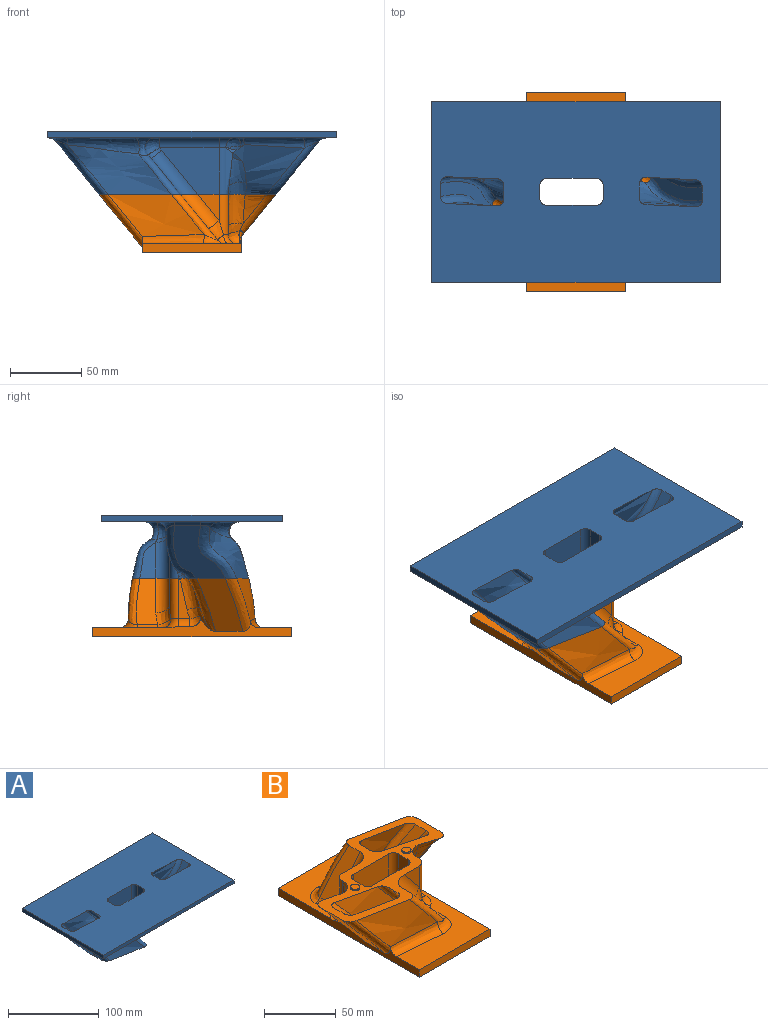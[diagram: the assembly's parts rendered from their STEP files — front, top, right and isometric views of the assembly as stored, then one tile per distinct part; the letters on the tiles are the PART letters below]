
ASSEMBLY  parts=2 mates=1
PART A: 89 faces, bbox 208.2x130.3x60.3 mm
  f0: plane 203.2x127mm, normal (0,0,-1), area 16715.4mm2, adj f4,f5,f6,f7,f62,f63,f64,f65
  f1: plane 27.1x22.42mm, normal (-0.78,0,0.63), area 270.1mm2, adj f20,f60,f84
  f2: bspline ~26.47x26.15mm, area 3.7mm2, adj f25,f52,f74
  f3: plane 0.85x0.52mm, normal (-1,0,0), area 0.2mm2, adj f11,f54,f84
  f4: plane 203.2x4.75mm, normal (0,1,0), area 965.2mm2, adj f0,f5,f7,f8
  f5: plane 127x4.75mm, normal (1,0,0), area 603.2mm2, adj f0,f4,f6,f8
  f6: plane 203.2x4.75mm, normal (0,-1,0), area 965.2mm2, adj f0,f5,f7,f8
  f7: plane 127x4.75mm, normal (-1,0,0), area 603.2mm2, adj f0,f4,f6,f8
  f8: plane 203.45x127.25mm, normal (0,0,1), area 23325.4mm2, adj f4,f5,f6,f7,f28,f29,f30,f31
  f9: cylinder r=6.35mm len=32.72mm, axis (0,0,-1), area 257.4mm2, adj f10,f13,f57,f58,f75,f84
  f10: plane 41.74x32.72mm, normal (0,-1,0), area 926.6mm2, adj f9,f55,f56,f77,f84
  f11: cylinder r=6.35mm len=32.72mm, axis (0,0,-1), area 241.2mm2, adj f3,f12,f52,f53,f70,f84
  f12: plane 41.72x32.72mm, normal (0,1,0), area 926.6mm2, adj f11,f60,f61,f68,f84
  f13: plane 4.33x2.1mm, normal (1,0,0), area 4.6mm2, adj f9,f59,f84
  f14: bspline ~26.57x26.16mm, area 3.1mm2, adj f15,f57,f71
  f15: bspline ~81.71x47.4mm, area 1132.1mm2, adj f14,f16,f58,f59,f69,f84
  f16: bspline ~51.16x47.96mm, area 420.9mm2, adj f15,f17,f67,f84
  f17: plane 37.97x37.8mm, normal (0.78,0,-0.63), area 979.7mm2, adj f16,f18,f65,f84
  f18: bspline ~52.84x48.18mm, area 451.5mm2, adj f17,f19,f63,f84
  f19: bspline ~85.74x51.46mm, area 1511.6mm2, adj f18,f20,f62,f84
  f20: bspline ~31.16x30.47mm, area 324.5mm2, adj f1,f19,f61,f64,f84
  f21: bspline ~53.3x48.55mm, area 461.5mm2, adj f22,f27,f82,f84
  f22: bspline ~80.68x45.46mm, area 1516.6mm2, adj f21,f26,f83,f84
  f23: plane 27.06x22.41mm, normal (0.78,0,0.63), area 191.7mm2, adj f26,f55,f84
  f24: bspline ~50.92x47.77mm, area 424.9mm2, adj f25,f27,f78,f84
  f25: bspline ~84.85x50.64mm, area 1089.3mm2, adj f2,f24,f53,f54,f76,f84
  f26: bspline ~31.1x30.41mm, area 312.9mm2, adj f22,f23,f56,f81,f84
  f27: plane 38.12x36.94mm, normal (-0.78,0,-0.63), area 981.5mm2, adj f21,f24,f80,f84
  f28: plane 44.45x9.53mm, normal (1,0,0), area 423.4mm2, adj f8,f29,f35,f84
  f29: cylinder r=4.76mm len=44.45mm, axis (0,0,-1), area 332.5mm2, adj f8,f28,f30,f84
  f30: plane 44.45x34.93mm, normal (0,-1,0), area 1552.4mm2, adj f8,f29,f31,f84
  f31: cylinder r=4.76mm len=44.45mm, axis (0,0,-1), area 332.5mm2, adj f8,f30,f32,f84
  f32: plane 44.45x9.53mm, normal (-1,0,0), area 423.4mm2, adj f8,f31,f33,f84
  f33: cylinder r=4.76mm len=44.45mm, axis (0,0,-1), area 332.5mm2, adj f8,f32,f34,f84
  f34: plane 44.45x34.93mm, normal (0,1,0), area 1552.4mm2, adj f8,f33,f35,f84
  f35: cylinder r=4.76mm len=44.45mm, axis (0,0,-1), area 332.5mm2, adj f8,f28,f34,f84
  f36: bspline ~80.13x56.1mm, area 1676.3mm2, adj f8,f37,f39,f84
  f37: bspline ~45.96x41.08mm, area 416.8mm2, adj f8,f36,f38,f84
  f38: plane 45.43x37.2mm, normal (-0.78,0,-0.63), area 587.4mm2, adj f8,f37,f40,f84
  f39: bspline ~56.3x50.6mm, area 399.9mm2, adj f8,f36,f43,f84
  f40: bspline ~53.19x48.1mm, area 414.1mm2, adj f8,f38,f41,f84
  f41: bspline ~77.52x52.9mm, area 1682.4mm2, adj f8,f40,f42,f84
  f42: bspline ~45.92x40.98mm, area 421.9mm2, adj f8,f41,f43,f84
  f43: plane 45.21x36.98mm, normal (0.78,0,0.63), area 581.6mm2, adj f8,f39,f42,f84
  f44: bspline ~74.38x49.37mm, area 1685mm2, adj f8,f45,f49,f84
  f45: bspline ~55.24x49.24mm, area 420mm2, adj f8,f44,f46,f84
  f46: plane 44.91x36.68mm, normal (0.78,0,-0.63), area 598.6mm2, adj f8,f45,f50,f84
  f47: bspline ~46.01x40.98mm, area 419.8mm2, adj f8,f48,f51,f84
  f48: plane 45.17x36.93mm, normal (-0.78,0,0.63), area 580.4mm2, adj f8,f47,f49,f84
  f49: bspline ~49.59x45.11mm, area 399.8mm2, adj f8,f44,f48,f84
  f50: bspline ~45.74x42.03mm, area 421.3mm2, adj f8,f46,f51,f84
  f51: bspline ~77.16x52.45mm, area 1689.8mm2, adj f8,f47,f50,f84
  f52: bspline ~10.59x8.46mm, area 46mm2, adj f2,f11,f53,f72
  f53: bspline ~32.83x16.02mm, area 369.8mm2, adj f11,f25,f52,f54
  f54: bspline ~13.55x12.77mm, area 82.6mm2, adj f3,f25,f53,f84
  f55: cylinder r=9.53mm len=37.14mm, axis (0.63,0,-0.78), area 542.6mm2, adj f10,f23,f56,f84
  f56: bspline ~19.85x18.08mm, area 39.9mm2, adj f10,f26,f55,f79
  f57: bspline ~11.14x7.85mm, area 43.8mm2, adj f9,f14,f73
  f58: bspline ~29.23x17.21mm, area 0mm2, adj f9,f15,f59
  f59: bspline ~16.03x15.49mm, area 128.9mm2, adj f13,f15,f58,f84
  f60: cylinder r=9.53mm len=37.33mm, axis (-0.63,0,-0.78), area 546.2mm2, adj f1,f12,f61,f84
  f61: bspline ~19.57x17.96mm, area 37.4mm2, adj f12,f20,f60,f66
  f62: bspline ~68.57x22.97mm, area 645.5mm2, adj f0,f19,f63,f64
  f63: bspline ~15.03x14.25mm, area 125.7mm2, adj f0,f18,f62,f65
  f64: bspline ~22.36x20.15mm, area 163.7mm2, adj f0,f20,f62,f66
  f65: cylinder r=6.99mm len=18.5mm, axis (0,-1,0), area 114.6mm2, adj f0,f17,f63,f67
  f66: bspline ~22.78x12.09mm, area 162mm2, adj f0,f61,f64,f68
  f67: bspline ~16.67x12.75mm, area 143.1mm2, adj f0,f16,f65,f69
  f68: cylinder r=6.99mm len=41.71mm, axis (-1,0,0), area 457.7mm2, adj f0,f12,f66,f70
  f69: bspline ~58x14.02mm, area 427.1mm2, adj f0,f15,f67,f71
  f70: torus R=13.33mm, axis (0,0,-1), area 76.6mm2, adj f0,f11,f68,f72
  f71: bspline ~8.55x8.16mm, area 29.4mm2, adj f0,f14,f69,f73
  f72: bspline ~13.61x8.18mm, area 85.8mm2, adj f0,f52,f70,f74
  f73: bspline ~13.15x8.04mm, area 86.3mm2, adj f0,f57,f71,f75
  f74: bspline ~8.96x8.54mm, area 33.4mm2, adj f0,f2,f72,f76
  f75: torus R=13.33mm, axis (0,0,-1), area 82.6mm2, adj f0,f9,f73,f77
  f76: bspline ~62.1x14.39mm, area 444mm2, adj f0,f25,f74,f78
  f77: cylinder r=6.99mm len=41.73mm, axis (1,0,0), area 457.9mm2, adj f0,f10,f75,f79
  f78: bspline ~17.07x12.87mm, area 151.7mm2, adj f0,f24,f76,f80
  f79: bspline ~22.42x12.24mm, area 162.6mm2, adj f0,f56,f77,f81
  f80: cylinder r=6.99mm len=18.32mm, axis (0,1,0), area 113.5mm2, adj f0,f27,f78,f82
  f81: bspline ~21.42x20.29mm, area 158.4mm2, adj f0,f26,f79,f83
  f82: bspline ~13.99x13.25mm, area 108.2mm2, adj f0,f21,f80,f83
  f83: bspline ~65.57x22.1mm, area 631.4mm2, adj f0,f22,f81,f82
  f84: plane 127.7x85.1mm, normal (0,0,-1), area 2652.4mm2, adj f1,f3,f9,f10,f11,f12,f13,f15
  f85: cylinder r=3.24mm len=6.48mm, axis (0,0,-1), area 25.8mm2, adj f84,f86
  f86: plane 6.48x6.48mm, normal (0,0,-1), area 32.9mm2, adj f85
  f87: cylinder r=3.24mm len=6.48mm, axis (0,0,-1), area 25.8mm2, adj f84,f88
  f88: plane 6.48x6.48mm, normal (0,0,-1), area 32.9mm2, adj f87
PART B: 86 faces, bbox 138.6x145.9x60.1 mm
  f0: plane 34.07x28.03mm, normal (-0.78,0,0.63), area 551.8mm2, adj f12,f47,f60,f76,f81
  f1: plane 28.58x7.98mm, normal (-1,0,0), area 124.8mm2, adj f4,f44,f56,f79,f81
  f2: cylinder r=6.35mm len=28.58mm, axis (0,0,-1), area 267.3mm2, adj f3,f6,f58,f66,f81
  f3: plane 18.4x15mm, normal (0,-1,0), area 138mm2, adj f2,f45,f81
  f4: cylinder r=6.35mm len=28.58mm, axis (0,0,-1), area 267.3mm2, adj f1,f5,f60,f78,f81
  f5: plane 18.4x15mm, normal (0,1,0), area 138mm2, adj f4,f47,f81
  f6: plane 28.58x9.56mm, normal (1,0,0), area 175.1mm2, adj f2,f46,f59,f67,f81
  f7: bspline ~71.62x36.76mm, area 148.8mm2, adj f8,f46,f81
  f8: bspline ~35.61x35.36mm, area 328.6mm2, adj f7,f9,f48,f59,f69,f70,f81
  f9: plane 31.39x28.84mm, normal (0.78,0,-0.63), area 729.1mm2, adj f8,f10,f71,f81
  f10: bspline ~41.65x39.28mm, area 332.3mm2, adj f9,f11,f72,f73,f81
  f11: bspline ~78.13x42.84mm, area 1296.3mm2, adj f10,f12,f74,f81
  f12: bspline ~43.2x41.45mm, area 338.4mm2, adj f0,f11,f75,f81
  f13: bspline ~44.38x41.67mm, area 406.6mm2, adj f14,f19,f53,f61,f81
  f14: bspline ~78.13x42.58mm, area 1314.4mm2, adj f13,f18,f62,f81
  f15: plane 33.62x27.59mm, normal (0.78,0,0.63), area 505mm2, adj f18,f45,f58,f64,f81
  f16: bspline ~44.1x42.28mm, area 393.2mm2, adj f17,f19,f53,f56,f57,f81
  f17: bspline ~73.56x38.12mm, area 153.6mm2, adj f16,f44,f81
  f18: bspline ~33.97x33.89mm, area 344.3mm2, adj f14,f15,f63,f81
  f19: plane 38.07x33.47mm, normal (-0.78,0,-0.63), area 950.1mm2, adj f13,f16,f53,f81
  f20: plane 41.28x9.53mm, normal (1,0,0), area 393.1mm2, adj f21,f27,f55,f81
  f21: cylinder r=4.76mm len=41.28mm, axis (0,0,-1), area 308.8mm2, adj f20,f22,f55,f81
  f22: plane 41.28x34.93mm, normal (0,-1,0), area 1441.5mm2, adj f21,f23,f55,f81
  f23: cylinder r=4.76mm len=41.28mm, axis (0,0,-1), area 308.8mm2, adj f22,f24,f55,f81
  f24: plane 41.28x9.53mm, normal (-1,0,0), area 393.1mm2, adj f23,f25,f55,f81
  f25: cylinder r=4.76mm len=41.28mm, axis (0,0,-1), area 308.8mm2, adj f24,f26,f55,f81
  f26: plane 41.28x34.93mm, normal (0,1,0), area 1441.5mm2, adj f25,f27,f55,f81
  f27: cylinder r=4.76mm len=41.28mm, axis (0,0,-1), area 308.8mm2, adj f20,f26,f55,f81
  f28: bspline ~71.59x46.22mm, area 1469.1mm2, adj f29,f31,f55,f81
  f29: bspline ~42.6x38.39mm, area 366.4mm2, adj f28,f30,f55,f81
  f30: plane 43.07x35.43mm, normal (-0.78,0,-0.63), area 508mm2, adj f29,f32,f55,f81
  f31: bspline ~46.27x42.41mm, area 368.2mm2, adj f28,f35,f55,f81
  f32: bspline ~42.27x39.21mm, area 348.7mm2, adj f30,f33,f55,f81
  f33: bspline ~76.28x51.98mm, area 1464.1mm2, adj f32,f34,f55,f81
  f34: bspline ~49.97x44.88mm, area 361.9mm2, adj f33,f35,f55,f81
  f35: plane 42.93x35.29mm, normal (0.78,0,0.63), area 520.7mm2, adj f31,f34,f55,f81
  f36: bspline ~70.56x45.46mm, area 1465.9mm2, adj f37,f41,f55,f81
  f37: bspline ~42.77x38.39mm, area 367.3mm2, adj f36,f38,f55,f81
  f38: plane 42.44x34.8mm, normal (0.78,0,-0.63), area 503.9mm2, adj f37,f42,f55,f81
  f39: bspline ~46x41.67mm, area 362.2mm2, adj f40,f43,f55,f81
  f40: plane 42.35x34.71mm, normal (-0.78,0,0.63), area 521mm2, adj f39,f41,f55,f81
  f41: bspline ~45.13x41.53mm, area 366.2mm2, adj f36,f40,f55,f81
  f42: bspline ~47.25x43.18mm, area 345mm2, adj f38,f43,f55,f81
  f43: bspline ~72.41x47.16mm, area 1459.6mm2, adj f39,f42,f55,f81
  f44: bspline ~36.3x17.53mm, area 372.1mm2, adj f1,f17,f56,f81
  f45: cylinder r=9.53mm len=30.44mm, axis (0.63,0,-0.78), area 413.2mm2, adj f3,f15,f58,f81
  f46: bspline ~30.53x16.91mm, area 377.5mm2, adj f6,f7,f59,f81
  f47: cylinder r=9.53mm len=30.44mm, axis (-0.63,0,-0.78), area 413.2mm2, adj f0,f5,f60,f81
  f48: bspline ~9.58x9.14mm, area 38.6mm2, adj f8,f51,f69,f70
  f49: plane 69.85x51.92mm, normal (0,0,1), area 1597.7mm2, adj f50,f51,f53,f73,f74,f75,f76,f77
  f50: plane 69.85x6.35mm, normal (0,1,0), area 443.5mm2, adj f49,f51,f53,f55
  f51: plane 141.87x8.52mm, normal (1,0,0), area 887.1mm2, adj f48,f49,f50,f52,f54,f55,f70,f71
  f52: plane 69.85x6.35mm, normal (0,-1,0), area 443.5mm2, adj f51,f53,f54,f55
  f53: plane 145.87x20.76mm, normal (-1,0,0), area 874.1mm2, adj f13,f16,f19,f49,f50,f52,f54,f55
  f54: plane 73.36x69.85mm, normal (0,0,1), area 1896.1mm2, adj f51,f52,f53,f62,f63,f64,f65,f66
  f55: plane 139.86x70.01mm, normal (0,0,-1), area 7276.1mm2, adj f20,f21,f22,f23,f24,f25,f26,f27
  f56: bspline ~23.27x17.29mm, area 127mm2, adj f1,f16,f44,f53,f57,f80
  f57: bspline ~9.86x6.75mm, area 0mm2, adj f16,f53,f56
  f58: bspline ~16.19x10.7mm, area 134.1mm2, adj f2,f15,f45,f65
  f59: bspline ~12.48x11.61mm, area 92.4mm2, adj f6,f8,f46,f68
  f60: bspline ~16.19x10.7mm, area 134.1mm2, adj f0,f4,f47,f77
  f61: bspline ~6.31x5.42mm, area 0.1mm2, adj f13,f53,f62
  f62: bspline ~60.55x11.2mm, area 414.7mm2, adj f14,f53,f54,f61,f63
  f63: bspline ~15.39x12.69mm, area 124.3mm2, adj f18,f54,f62,f64
  f64: cylinder r=6.35mm len=14.54mm, axis (0,-1,0), area 81.9mm2, adj f15,f54,f63,f65
  f65: bspline ~10.92x7.6mm, area 58.8mm2, adj f54,f58,f64,f66
  f66: torus R=12.7mm, axis (0,0,-1), area 88.2mm2, adj f2,f54,f65,f67
  f67: cylinder r=6.35mm len=9.56mm, axis (0,-1,0), area 95.3mm2, adj f6,f54,f66,f68
  f68: bspline ~13.97x10.1mm, area 119.2mm2, adj f54,f59,f67,f69
  f69: bspline ~10.04x9.04mm, area 5.3mm2, adj f8,f48,f54,f68
  f70: bspline ~7.54x5.65mm, area 22.5mm2, adj f8,f48,f51,f71
  f71: cylinder r=6.35mm len=19.32mm, axis (0,-1,0), area 132.8mm2, adj f9,f51,f70,f72
  f72: bspline ~11.91x7.7mm, area 60.7mm2, adj f10,f51,f71,f73
  f73: bspline ~8.79x7.66mm, area 45.2mm2, adj f10,f49,f72,f74
  f74: bspline ~53.23x9.96mm, area 429.2mm2, adj f11,f49,f73,f75
  f75: bspline ~15.43x12.6mm, area 128.4mm2, adj f12,f49,f74,f76
  f76: cylinder r=6.35mm len=14.66mm, axis (0,1,0), area 82.6mm2, adj f0,f49,f75,f77
  f77: bspline ~10.92x7.6mm, area 58.8mm2, adj f49,f60,f76,f78
  f78: torus R=12.7mm, axis (0,0,-1), area 74.3mm2, adj f4,f49,f53,f77,f79
  f79: cylinder r=6.35mm len=7.98mm, axis (0,1,0), area 53mm2, adj f1,f53,f78,f80
  f80: bspline ~10.97x8.43mm, area 25.7mm2, adj f53,f56,f79
  f81: plane 127.7x85.1mm, normal (0,0,1), area 2655mm2, adj f0,f1,f2,f3,f4,f5,f6,f7
  f82: cylinder r=3.17mm len=6.35mm, axis (0,0,-1), area 25.3mm2, adj f81,f83
  f83: plane 6.35x6.35mm, normal (0,0,1), area 31.7mm2, adj f82
  f84: cylinder r=3.17mm len=6.35mm, axis (0,0,-1), area 25.3mm2, adj f81,f85
  f85: plane 6.35x6.35mm, normal (0,0,1), area 31.7mm2, adj f84
PLACE A t=(-17.74,56.43,37.34)mm
PLACE B t=(-17.74,56.43,37.34)mm
MATE fastened B.f84 <-> A.f85  axis (0,0,1) through (7.66,59.61,79.88)mm
